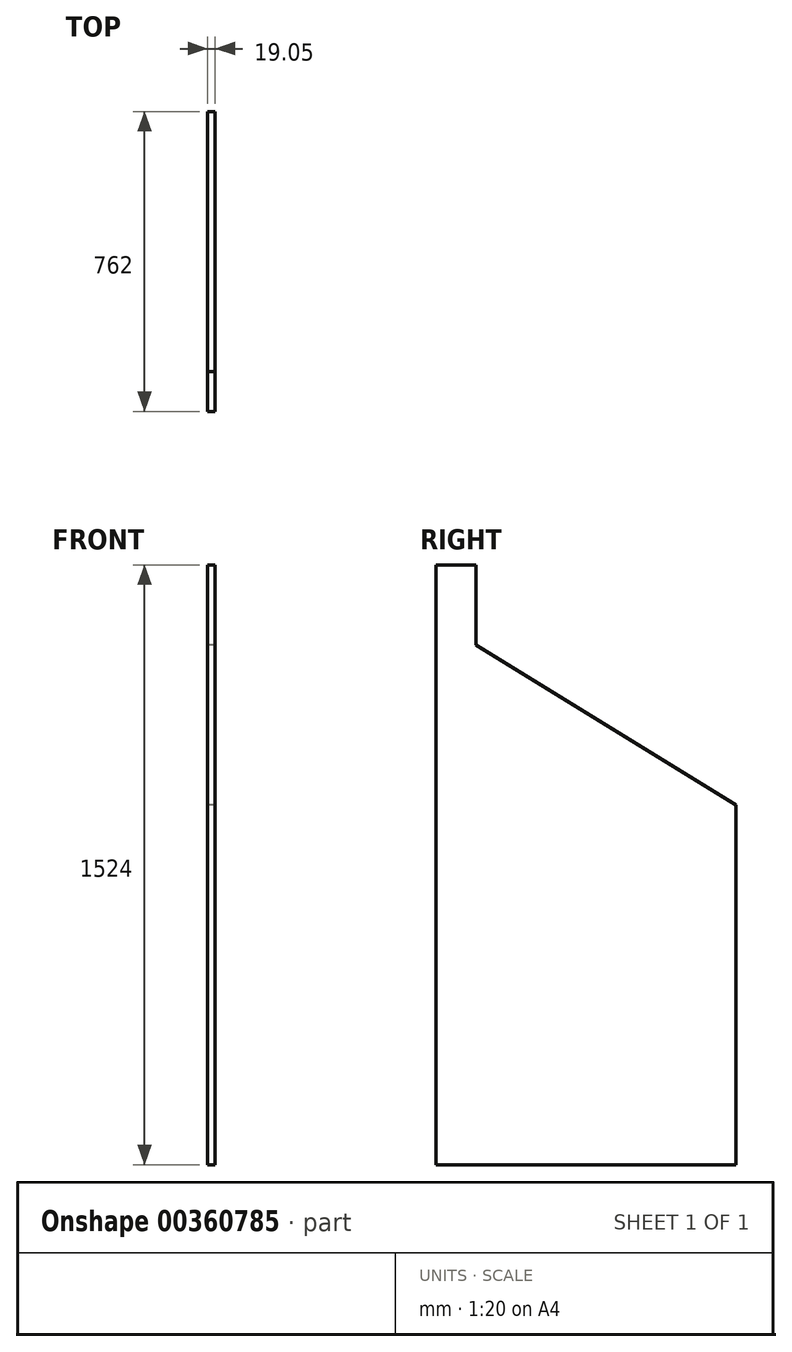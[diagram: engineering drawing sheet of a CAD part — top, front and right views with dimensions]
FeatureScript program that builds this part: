
annotation { "Feature Type Name" : "Feature", "Feature Type Description" : "" }
export const myFeature = defineFeature(function(context is Context, id is Id, definition is map)
    precondition{}
    {
        {
            var Q0;
            Q0=qCreatedBy(makeId("Right.planeOp"),FACE);
            var sketch = newSketch(context, id + "F0", { "sketchPlane" : qUnion([Q0])});
            skLineSegment(sketch, "E0", {"start": v(0, 0) * mm, "end": v(0, 1524) * mm});
            skLineSegment(sketch, "E1", {"start": v(0, 0) * mm, "end": v(762, 0) * mm});
            skLineSegment(sketch, "E2", {"start": v(0, 1524) * mm, "end": v(101.6, 1524) * mm});
            skLineSegment(sketch, "E3", {"start": v(101.6, 1524) * mm, "end": v(101.6, 1524) * mm});
            skLineSegment(sketch, "E4", {"start": v(101.6, 1320.8) * mm, "end": v(101.6, 1524) * mm});
            skLineSegment(sketch, "E5", {"start": v(762, 914.4) * mm, "end": v(762, 0) * mm});
            skLineSegment(sketch, "E6", {"start": v(762, 914.4) * mm, "end": v(101.6, 1320.8) * mm});
            skSolve(sketch);
        }
        {
            var Q0;
            Q0=makeQuery(id+"F0.imprint","IMPRINT",FACE,{"disambiguationData":[TD([[makeQuery(id+"F0.imprint","IMPRINT",EDGE,{"derivedFrom":sQuery(id+"F0.wireOp",EDGE,"E0")}),-1.0]])]});
            extrude(context, id + "F1", {"entities" : qUnion([Q0]), "depth" : 19.05 * mm});
        }
    });
